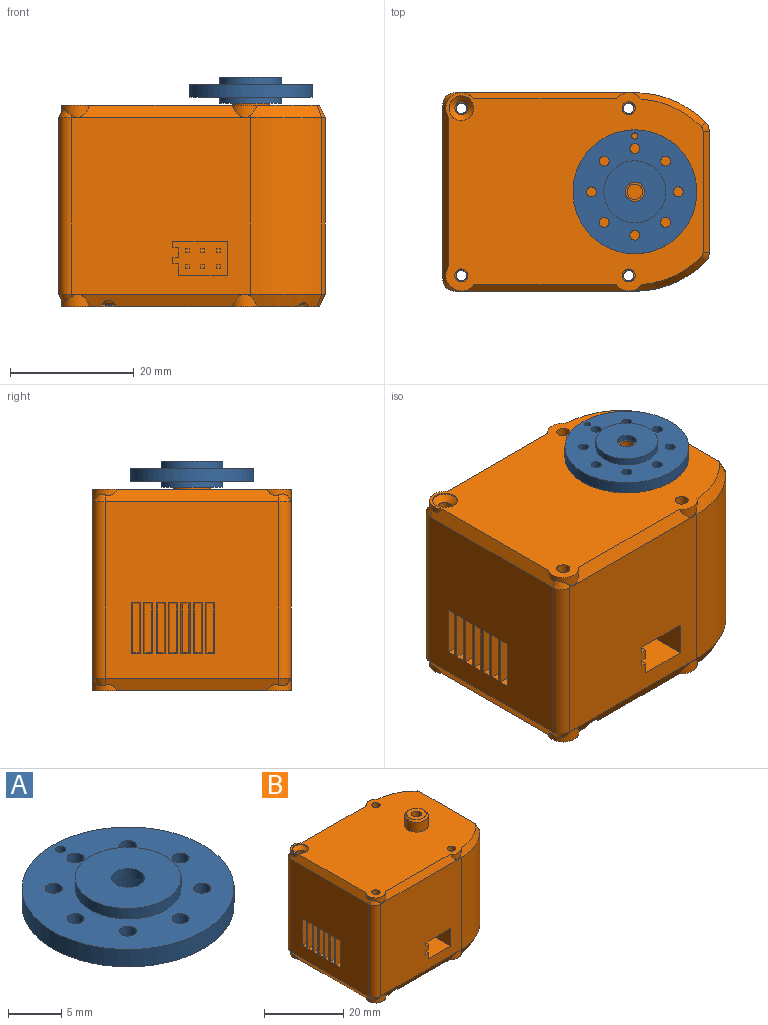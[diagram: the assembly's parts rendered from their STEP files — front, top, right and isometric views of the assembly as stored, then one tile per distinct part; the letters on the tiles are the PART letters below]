
ASSEMBLY  parts=2 mates=1
PART A: 19 faces, bbox 20x20x4.2 mm
  f0: cylinder r=5mm len=10mm, axis (0,0,-1), area 31.4mm2, adj f1,f5
  f1: plane 10x10mm, normal (0,0,-1), area 50.3mm2, adj f0,f8
  f2: cylinder r=5mm len=10mm, axis (0,0,1), area 37.7mm2, adj f3,f6
  f3: plane 10x10mm, normal (0,0,1), area 71mm2, adj f2,f7
  f4: cylinder r=10mm len=20mm, axis (0,0,1), area 125.7mm2, adj f5,f6
  f5: plane 20x20mm, normal (0,0,-1), area 218.7mm2, adj f0,f4,f10,f11,f12,f13,f14,f15
  f6: plane 20x20mm, normal (0,0,1), area 218.7mm2, adj f2,f4,f10,f11,f12,f13,f14,f15
  f7: cylinder r=1.55mm len=3.1mm, axis (0,0,1), area 9.7mm2, adj f3,f9
  f8: cylinder r=3mm len=6mm, axis (0,0,1), area 60.3mm2, adj f1,f9
  f9: plane 6x6mm, normal (0,0,-1), area 20.7mm2, adj f7,f8
  f10: cylinder r=0.8mm len=2mm, axis (0,0,1), area 10.1mm2, adj f5,f6
  f11: cylinder r=0.5mm len=2mm, axis (0,0,1), area 6.3mm2, adj f5,f6
  f12: cylinder r=0.8mm len=2mm, axis (0,0,1), area 10.1mm2, adj f5,f6
  f13: cylinder r=0.8mm len=2mm, axis (0,0,1), area 10.1mm2, adj f5,f6
  f14: cylinder r=0.8mm len=2mm, axis (0,0,1), area 10.1mm2, adj f5,f6
  f15: cylinder r=0.8mm len=2mm, axis (0,0,1), area 10.1mm2, adj f5,f6
  f16: cylinder r=0.8mm len=2mm, axis (0,0,1), area 10.1mm2, adj f5,f6
  f17: cylinder r=0.8mm len=2mm, axis (0,0,1), area 10.1mm2, adj f5,f6
  f18: cylinder r=0.8mm len=2mm, axis (0,0,1), area 10.1mm2, adj f5,f6
PART B: 273 faces, bbox 43.9x32.9x36.9 mm
  f0: cylinder r=1.05mm len=8mm, axis (0,0,-1), area 52.8mm2, adj f30,f40
  f1: cylinder r=1.05mm len=8mm, axis (0,0,-1), area 52.8mm2, adj f30,f41
  f2: cylinder r=2mm len=4mm, axis (0,0,1), area 2.5mm2, adj f6,f30
  f3: cylinder r=1.05mm len=8mm, axis (0,0,-1), area 52.8mm2, adj f30,f42
  f4: cylinder r=3mm len=6mm, axis (0,0,1), area 56.5mm2, adj f30,f43,f44
  f5: cylinder r=2.5mm len=4.5mm, axis (0,0,-1), area 8.1mm2, adj f30,f31,f32,f46,f47
  f6: cone r=1000mm half-angle=45deg, axis (0,0,1), area 12.9mm2, adj f2,f9
  f7: cylinder r=0.85mm len=20.8mm, axis (0,0,1), area 111.1mm2, adj f40,f64
  f8: cylinder r=0.85mm len=20.8mm, axis (0,0,1), area 111.1mm2, adj f41,f65
  f9: cylinder r=1.05mm len=6.85mm, axis (0,0,-1), area 45.2mm2, adj f6,f66
  f10: cylinder r=0.85mm len=20.8mm, axis (0,0,1), area 111.1mm2, adj f42,f67
  f11: cylinder r=1.25mm len=9mm, axis (0,0,-1), area 70.7mm2, adj f59,f120
  f12: cylinder r=1.05mm len=3.7mm, axis (0,0,-1), area 24.4mm2, adj f64,f146
  f13: cylinder r=1.05mm len=3.7mm, axis (0,0,-1), area 24.4mm2, adj f65,f146
  f14: cylinder r=0.85mm len=20.8mm, axis (0,0,1), area 111.1mm2, adj f66,f147
  f15: cylinder r=1.05mm len=3.7mm, axis (0,0,-1), area 24.4mm2, adj f67,f146
  f16: cylinder r=2mm len=4mm, axis (0,0,-1), area 17.4mm2, adj f135,f146,f164
  f17: cylinder r=2mm len=4mm, axis (0,0,-1), area 17.8mm2, adj f137,f146,f165
  f18: cylinder r=2mm len=4mm, axis (0,0,-1), area 18.8mm2, adj f139,f146,f166
  f19: cylinder r=2mm len=4mm, axis (0,0,-1), area 17.4mm2, adj f144,f146,f187
  f20: cylinder r=4.25mm len=8.5mm, axis (0,0,-1), area 13.4mm2, adj f146,f188
  f21: cylinder r=2mm len=4mm, axis (0,0,-1), area 2.5mm2, adj f23,f146
  f22: cylinder r=1.05mm len=2.55mm, axis (0,0,-1), area 16.8mm2, adj f23,f147
  f23: cone r=1000mm half-angle=45deg, axis (0,0,-1), area 12.9mm2, adj f21,f22
  f24: cylinder r=1.75mm len=3.5mm, axis (0,0,-1), area 2.2mm2, adj f164,f195,f196
  f25: cylinder r=1.75mm len=3.5mm, axis (0,0,-1), area 2.2mm2, adj f165,f197,f198
  f26: cylinder r=1.75mm len=3.5mm, axis (0,0,-1), area 2.2mm2, adj f166,f199,f200
  f27: cylinder r=1.75mm len=3.5mm, axis (0,0,-1), area 2.2mm2, adj f187,f201,f202
  f28: cylinder r=2.7mm len=5.4mm, axis (0,0,-1), area 8.5mm2, adj f188,f203
  f29: cylinder r=1.2mm len=10mm, axis (0,0,-1), area 75.4mm2, adj f203,f272
  f30: plane 41.5x32mm, normal (0,0,1), area 1159.4mm2, adj f0,f1,f2,f3,f4,f5,f31,f32
  f31: plane 28.86x2.86mm, normal (-0.89,0,0.45), area 59.2mm2, adj f5,f30,f39,f45,f46,f58
  f32: plane 27.94x2.94mm, normal (0,0.89,0.45), area 54.1mm2, adj f5,f30,f33,f48
  f33: cylinder r=2.5mm len=4.03mm, axis (0,0,-1), area 5.2mm2, adj f30,f32,f34,f49
  f34: cone r=14.9mm half-angle=26.6deg, axis (0,0,-1), area 26.7mm2, adj f30,f33,f49,f50,f51
  f35: plane 19.6x2mm, normal (0.89,0,0.45), area 43.8mm2, adj f30,f51,f52,f53
  f36: cone r=14.9mm half-angle=26.6deg, axis (0,0,-1), area 26.7mm2, adj f30,f37,f52,f54,f55
  f37: cylinder r=2.5mm len=4.03mm, axis (0,0,-1), area 5.2mm2, adj f30,f36,f38,f55
  f38: plane 27.94x2.94mm, normal (0,-0.89,0.45), area 54.1mm2, adj f30,f37,f39,f56
  f39: cylinder r=2.5mm len=4.5mm, axis (0,0,-1), area 8.1mm2, adj f30,f31,f38,f57,f58
  f40: plane 2.1x2.1mm, normal (0,0,1), area 1.2mm2, adj f0,f7
  f41: plane 2.1x2.1mm, normal (0,0,1), area 1.2mm2, adj f1,f8
  f42: plane 2.1x2.1mm, normal (0,0,1), area 1.2mm2, adj f3,f10
  f43: revolved ~6x3mm, area 6.1mm2, adj f4,f44,f59
  f44: revolved ~6x3mm, area 6.1mm2, adj f4,f43,f59
  f45: plane 28.5x28mm, normal (-1,0,0), area 713.8mm2, adj f31,f60,f61,f68,f69,f70,f71,f72
  f46: cone r=1.16mm half-angle=26.6deg, axis (0,0,-1), area 3.1mm2, adj f5,f31,f47,f61
  f47: plane 1.21x0.62mm, normal (0,0.89,0.45), area 0.2mm2, adj f5,f46,f48
  f48: plane 29x28.5mm, normal (0,1,0), area 766.3mm2, adj f32,f47,f49,f50,f61,f96,f97,f98
  f49: plane 1.21x0.62mm, normal (0,0.89,0.45), area 0.2mm2, adj f33,f34,f48
  f50: cylinder r=16mm len=28.5mm, axis (0,0,-1), area 362.8mm2, adj f34,f48,f62,f137
  f51: cone r=1.16mm half-angle=26.6deg, axis (0,0,-1), area 2.6mm2, adj f30,f34,f35,f62
  f52: cone r=1.16mm half-angle=26.6deg, axis (0,0,-1), area 2.6mm2, adj f30,f35,f36,f63
  f53: plane 28.5x19.6mm, normal (1,0,0), area 558.5mm2, adj f35,f62,f63,f138
  f54: cylinder r=16mm len=28.5mm, axis (0,0,-1), area 362.8mm2, adj f36,f56,f63,f139
  f55: plane 1.21x0.62mm, normal (0,-0.89,0.45), area 0.2mm2, adj f36,f37,f56
  f56: plane 29x28.5mm, normal (0,-1,0), area 781.3mm2, adj f38,f54,f55,f57,f60,f116,f117,f118
  f57: plane 1.21x0.62mm, normal (0,-0.89,0.45), area 0.2mm2, adj f39,f56,f58
  f58: cone r=1.16mm half-angle=26.6deg, axis (0,0,-1), area 3.1mm2, adj f31,f39,f57,f60
  f59: plane 5x5mm, normal (0,0,1), area 14.7mm2, adj f11,f43,f44
  f60: cylinder r=2mm len=28.5mm, axis (0,0,-1), area 89.5mm2, adj f45,f56,f58,f148
  f61: cylinder r=2mm len=28.5mm, axis (0,0,-1), area 89.5mm2, adj f45,f46,f48,f151
  f62: cylinder r=2mm len=28.5mm, axis (0,0,-1), area 44.2mm2, adj f50,f51,f53,f153
  f63: cylinder r=2mm len=28.5mm, axis (0,0,-1), area 44.2mm2, adj f52,f53,f54,f154
  f64: plane 2.1x2.1mm, normal (0,0,-1), area 1.2mm2, adj f7,f12
  f65: plane 2.1x2.1mm, normal (0,0,-1), area 1.2mm2, adj f8,f13
  f66: plane 2.1x2.1mm, normal (0,0,1), area 1.2mm2, adj f9,f14
  f67: plane 2.1x2.1mm, normal (0,0,-1), area 1.2mm2, adj f10,f15
  f68: plane 1.7x1.46mm, normal (-0.1,0,-0.99), area 2.2mm2, adj f45,f69,f71,f121
  f69: plane 8.26x1.7mm, normal (-0.1,-0.99,0), area 13.8mm2, adj f45,f68,f70,f121
  f70: plane 1.7x1.46mm, normal (-0.1,0,0.99), area 2.2mm2, adj f45,f69,f71,f121
  f71: plane 8.26x1.7mm, normal (-0.1,0.99,0), area 13.8mm2, adj f45,f68,f70,f121
  f72: plane 1.7x1.46mm, normal (-0.1,0,-0.99), area 2.2mm2, adj f45,f73,f75,f122
  f73: plane 8.26x1.7mm, normal (-0.1,-0.99,0), area 13.8mm2, adj f45,f72,f74,f122
  f74: plane 1.7x1.46mm, normal (-0.1,0,0.99), area 2.2mm2, adj f45,f73,f75,f122
  f75: plane 8.26x1.7mm, normal (-0.1,0.99,0), area 13.8mm2, adj f45,f72,f74,f122
  f76: plane 1.7x1.46mm, normal (-0.1,0,-0.99), area 2.2mm2, adj f45,f77,f79,f123
  f77: plane 8.26x1.7mm, normal (-0.1,-0.99,0), area 13.8mm2, adj f45,f76,f78,f123
  f78: plane 1.7x1.46mm, normal (-0.1,0,0.99), area 2.2mm2, adj f45,f77,f79,f123
  f79: plane 8.26x1.7mm, normal (-0.1,0.99,0), area 13.8mm2, adj f45,f76,f78,f123
  f80: plane 1.7x1.46mm, normal (-0.1,0,-0.99), area 2.2mm2, adj f45,f81,f83,f124
  f81: plane 8.26x1.7mm, normal (-0.1,-0.99,0), area 13.8mm2, adj f45,f80,f82,f124
  f82: plane 1.7x1.46mm, normal (-0.1,0,0.99), area 2.2mm2, adj f45,f81,f83,f124
  f83: plane 8.26x1.7mm, normal (-0.1,0.99,0), area 13.8mm2, adj f45,f80,f82,f124
  f84: plane 1.7x1.46mm, normal (-0.1,0,-0.99), area 2.2mm2, adj f45,f85,f87,f125
  f85: plane 8.26x1.7mm, normal (-0.1,-0.99,0), area 13.8mm2, adj f45,f84,f86,f125
  f86: plane 1.7x1.46mm, normal (-0.1,0,0.99), area 2.2mm2, adj f45,f85,f87,f125
  f87: plane 8.26x1.7mm, normal (-0.1,0.99,0), area 13.8mm2, adj f45,f84,f86,f125
  f88: plane 1.7x1.46mm, normal (-0.1,0,-0.99), area 2.2mm2, adj f45,f89,f91,f126
  f89: plane 8.26x1.7mm, normal (-0.1,-0.99,0), area 13.8mm2, adj f45,f88,f90,f126
  f90: plane 1.7x1.46mm, normal (-0.1,0,0.99), area 2.2mm2, adj f45,f89,f91,f126
  f91: plane 8.26x1.7mm, normal (-0.1,0.99,0), area 13.8mm2, adj f45,f88,f90,f126
  f92: plane 8.26x1.7mm, normal (-0.1,0.99,0), area 13.8mm2, adj f45,f93,f95,f127
  f93: plane 1.7x1.46mm, normal (-0.1,0,-0.99), area 2.2mm2, adj f45,f92,f94,f127
  f94: plane 8.26x1.7mm, normal (-0.1,-0.99,0), area 13.8mm2, adj f45,f93,f95,f127
  f95: plane 1.7x1.46mm, normal (-0.1,0,0.99), area 2.2mm2, adj f45,f92,f94,f127
  f96: plane 8.26x1.7mm, normal (-0.99,0.1,0), area 13.8mm2, adj f48,f97,f99,f129
  f97: plane 1.7x1.46mm, normal (0,0.1,0.99), area 2.2mm2, adj f48,f96,f98,f129
  f98: plane 8.26x1.7mm, normal (0.99,0.1,0), area 13.8mm2, adj f48,f97,f99,f129
  f99: plane 1.7x1.46mm, normal (0,0.1,-0.99), area 2.2mm2, adj f48,f96,f98,f129
  f100: plane 8.26x1.7mm, normal (-0.99,0.1,0), area 13.8mm2, adj f48,f101,f103,f130
  f101: plane 1.7x1.46mm, normal (0,0.1,0.99), area 2.2mm2, adj f48,f100,f102,f130
  f102: plane 8.26x1.7mm, normal (0.99,0.1,0), area 13.8mm2, adj f48,f101,f103,f130
  f103: plane 1.7x1.46mm, normal (0,0.1,-0.99), area 2.2mm2, adj f48,f100,f102,f130
  f104: plane 8.26x1.7mm, normal (-0.99,0.1,0), area 13.8mm2, adj f48,f105,f107,f131
  f105: plane 1.7x1.46mm, normal (0,0.1,0.99), area 2.2mm2, adj f48,f104,f106,f131
  f106: plane 8.26x1.7mm, normal (0.99,0.1,0), area 13.8mm2, adj f48,f105,f107,f131
  f107: plane 1.7x1.46mm, normal (0,0.1,-0.99), area 2.2mm2, adj f48,f104,f106,f131
  f108: plane 8.26x1.7mm, normal (-0.99,0.1,0), area 13.8mm2, adj f48,f109,f111,f132
  f109: plane 1.7x1.46mm, normal (0,0.1,0.99), area 2.2mm2, adj f48,f108,f110,f132
  f110: plane 8.26x1.7mm, normal (0.99,0.1,0), area 13.8mm2, adj f48,f109,f111,f132
  f111: plane 1.7x1.46mm, normal (0,0.1,-0.99), area 2.2mm2, adj f48,f108,f110,f132
  f112: plane 1.7x1.46mm, normal (0,0.1,-0.99), area 2.2mm2, adj f48,f113,f115,f133
  f113: plane 8.26x1.7mm, normal (-0.99,0.1,0), area 13.8mm2, adj f48,f112,f114,f133
  f114: plane 1.7x1.46mm, normal (0,0.1,0.99), area 2.2mm2, adj f48,f113,f115,f133
  f115: plane 8.26x1.7mm, normal (0.99,0.1,0), area 13.8mm2, adj f48,f112,f114,f133
  f116: plane 14.2x1.9mm, normal (1,0,0), area 27mm2, adj f56,f117,f140,f141
  f117: plane 14.2x7.9mm, normal (0,0,1), area 112.2mm2, adj f56,f116,f118,f141
  f118: plane 14.2x5.5mm, normal (-1,0,0), area 78.1mm2, adj f56,f117,f119,f141
  f119: plane 14.2x8.8mm, normal (0,0,-1), area 125mm2, adj f56,f118,f141,f142
  f120: plane 2.5x2.5mm, normal (0,0,1), area 4.9mm2, adj f11
  f121: plane 7.9x1.1mm, normal (-1,0,0), area 8.7mm2, adj f68,f69,f70,f71
  f122: plane 7.9x1.1mm, normal (-1,0,0), area 8.7mm2, adj f72,f73,f74,f75
  f123: plane 7.9x1.1mm, normal (-1,0,0), area 8.7mm2, adj f76,f77,f78,f79
  f124: plane 7.9x1.1mm, normal (-1,0,0), area 8.7mm2, adj f80,f81,f82,f83
  f125: plane 7.9x1.1mm, normal (-1,0,0), area 8.7mm2, adj f84,f85,f86,f87
  f126: plane 7.9x1.1mm, normal (-1,0,0), area 8.7mm2, adj f88,f89,f90,f91
  f127: plane 7.9x1.1mm, normal (-1,0,0), area 8.7mm2, adj f92,f93,f94,f95
  f128: plane 28.86x2.86mm, normal (-0.89,0,-0.45), area 59.2mm2, adj f45,f146,f148,f149,f150,f151
  f129: plane 7.9x1.1mm, normal (0,1,0), area 8.7mm2, adj f96,f97,f98,f99
  f130: plane 7.9x1.1mm, normal (0,1,0), area 8.7mm2, adj f100,f101,f102,f103
  f131: plane 7.9x1.1mm, normal (0,1,0), area 8.7mm2, adj f104,f105,f106,f107
  f132: plane 7.9x1.1mm, normal (0,1,0), area 8.7mm2, adj f108,f109,f110,f111
  f133: plane 7.9x1.1mm, normal (0,1,0), area 8.7mm2, adj f112,f113,f114,f115
  f134: plane 1.21x0.62mm, normal (0,0.89,-0.45), area 0.2mm2, adj f48,f150,f151
  f135: plane 27.94x2.94mm, normal (0,0.89,-0.45), area 52.1mm2, adj f16,f48,f146,f150,f152
  f136: plane 1.21x0.62mm, normal (0,0.89,-0.45), area 0.2mm2, adj f48,f137,f152
  f137: cone r=14.9mm half-angle=26.6deg, axis (0,0,1), area 25.4mm2, adj f17,f50,f136,f146,f152,f153
  f138: plane 19.6x2mm, normal (0.89,0,-0.45), area 43.8mm2, adj f53,f146,f153,f154
  f139: cone r=14.9mm half-angle=26.6deg, axis (0,0,1), area 25.6mm2, adj f18,f54,f143,f146,f154,f155
  f140: plane 14.2x0.9mm, normal (0,0,1), area 12.8mm2, adj f56,f116,f141,f156
  f141: plane 8.8x5.5mm, normal (0,-1,0), area 42.8mm2, adj f116,f117,f118,f119,f140,f142,f156,f157
  f142: plane 14.2x1mm, normal (1,0,0), area 14.2mm2, adj f56,f119,f141,f163
  f143: plane 1.21x0.62mm, normal (0,-0.89,-0.45), area 0.2mm2, adj f56,f139,f155
  f144: plane 27.94x2.94mm, normal (0,-0.89,-0.45), area 52.1mm2, adj f19,f56,f146,f149,f155
  f145: plane 1.21x0.62mm, normal (0,-0.89,-0.45), area 0.2mm2, adj f56,f148,f149
  f146: plane 41.5x32mm, normal (0,0,-1), area 1083.4mm2, adj f12,f13,f15,f16,f17,f18,f19,f20
  f147: plane 2.1x2.1mm, normal (0,0,-1), area 1.2mm2, adj f14,f22
  f148: cone r=1.16mm half-angle=26.6deg, axis (0,0,1), area 3.1mm2, adj f60,f128,f145,f149
  f149: cylinder r=2.5mm len=4.5mm, axis (0,0,1), area 8.1mm2, adj f128,f144,f145,f146,f148
  f150: cylinder r=2.5mm len=4.5mm, axis (0,0,1), area 8.1mm2, adj f128,f134,f135,f146,f151
  f151: cone r=1.16mm half-angle=26.6deg, axis (0,0,1), area 3.1mm2, adj f61,f128,f134,f150
  f152: cylinder r=2.5mm len=4.03mm, axis (0,0,1), area 5.2mm2, adj f135,f136,f137,f146
  f153: cone r=1.16mm half-angle=26.6deg, axis (0,0,1), area 2.6mm2, adj f62,f137,f138,f146
  f154: cone r=1.16mm half-angle=26.6deg, axis (0,0,1), area 2.6mm2, adj f63,f138,f139,f146
  f155: cylinder r=2.5mm len=4.03mm, axis (0,0,1), area 5.2mm2, adj f139,f143,f144,f146
  f156: plane 14.2x1mm, normal (1,0,0), area 14.2mm2, adj f56,f140,f141,f167
  f157: plane 5.7x0.64mm, normal (-1,0,0), area 3.6mm2, adj f141,f168,f169,f170
  f158: plane 5.7x0.64mm, normal (-1,0,0), area 3.6mm2, adj f141,f171,f172,f173
  f159: plane 5.7x0.64mm, normal (-1,0,0), area 3.6mm2, adj f141,f174,f175,f176
  f160: plane 5.7x0.64mm, normal (-1,0,0), area 3.6mm2, adj f141,f177,f178,f179
  f161: plane 5.7x0.64mm, normal (-1,0,0), area 3.6mm2, adj f141,f180,f181,f182
  f162: plane 5.7x0.64mm, normal (0,0,-1), area 3.6mm2, adj f141,f183,f184,f185
  f163: plane 14.2x0.9mm, normal (0,0,1), area 12.8mm2, adj f56,f141,f142,f186
  f164: plane 4x4mm, normal (0,0,-1), area 2.9mm2, adj f16,f24
  f165: plane 4x4mm, normal (0,0,-1), area 2.9mm2, adj f17,f25
  f166: plane 4x4mm, normal (0,0,-1), area 2.9mm2, adj f18,f26
  f167: plane 14.2x0.9mm, normal (0,0,-1), area 12.8mm2, adj f56,f141,f156,f186
  f168: plane 5.7x0.64mm, normal (0,0,-1), area 3.6mm2, adj f141,f157,f170,f189
  f169: plane 5.7x0.64mm, normal (0,0,1), area 3.6mm2, adj f141,f157,f170,f189
  f170: plane 0.64x0.64mm, normal (0,-1,0), area 0.4mm2, adj f157,f168,f169,f189
  f171: plane 5.7x0.64mm, normal (0,0,-1), area 3.6mm2, adj f141,f158,f173,f190
  f172: plane 5.7x0.64mm, normal (0,0,1), area 3.6mm2, adj f141,f158,f173,f190
  f173: plane 0.64x0.64mm, normal (0,-1,0), area 0.4mm2, adj f158,f171,f172,f190
  f174: plane 5.7x0.64mm, normal (0,0,-1), area 3.6mm2, adj f141,f159,f176,f191
  f175: plane 5.7x0.64mm, normal (0,0,1), area 3.6mm2, adj f141,f159,f176,f191
  f176: plane 0.64x0.64mm, normal (0,-1,0), area 0.4mm2, adj f159,f174,f175,f191
  f177: plane 5.7x0.64mm, normal (0,0,-1), area 3.6mm2, adj f141,f160,f179,f192
  f178: plane 5.7x0.64mm, normal (0,0,1), area 3.6mm2, adj f141,f160,f179,f192
  f179: plane 0.64x0.64mm, normal (0,-1,0), area 0.4mm2, adj f160,f177,f178,f192
  f180: plane 5.7x0.64mm, normal (0,0,-1), area 3.6mm2, adj f141,f161,f182,f193
  f181: plane 5.7x0.64mm, normal (0,0,1), area 3.6mm2, adj f141,f161,f182,f193
  f182: plane 0.64x0.64mm, normal (0,-1,0), area 0.4mm2, adj f161,f180,f181,f193
  f183: plane 5.7x0.64mm, normal (1,0,0), area 3.6mm2, adj f141,f162,f185,f194
  f184: plane 5.7x0.64mm, normal (-1,0,0), area 3.6mm2, adj f141,f162,f185,f194
  f185: plane 0.64x0.64mm, normal (0,-1,0), area 0.4mm2, adj f162,f183,f184,f194
  f186: plane 14.2x1.6mm, normal (1,0,0), area 22.7mm2, adj f56,f141,f163,f167
  f187: plane 4x4mm, normal (0,0,-1), area 2.9mm2, adj f19,f27
  f188: plane 8.5x8.5mm, normal (0,0,-1), area 33.8mm2, adj f20,f28
  f189: plane 5.7x0.64mm, normal (1,0,0), area 3.6mm2, adj f141,f168,f169,f170
  f190: plane 5.7x0.64mm, normal (1,0,0), area 3.6mm2, adj f141,f171,f172,f173
  f191: plane 5.7x0.64mm, normal (1,0,0), area 3.6mm2, adj f141,f174,f175,f176
  f192: plane 5.7x0.64mm, normal (1,0,0), area 3.6mm2, adj f141,f177,f178,f179
  f193: plane 5.7x0.64mm, normal (1,0,0), area 3.6mm2, adj f141,f180,f181,f182
  f194: plane 5.7x0.64mm, normal (0,0,1), area 3.6mm2, adj f141,f183,f184,f185
  f195: torus R=0.75mm, axis (0,0,1), area 6mm2, adj f24,f196,f204,f205,f206,f207,f208,f209
  f196: torus R=0.75mm, axis (0,0,1), area 6mm2, adj f24,f195,f209,f210,f213,f214,f215,f216
  f197: torus R=0.75mm, axis (0,0,1), area 6mm2, adj f25,f198,f220,f221,f222,f223,f224,f225
  f198: torus R=0.75mm, axis (0,0,1), area 6mm2, adj f25,f197,f225,f226,f229,f230,f231,f232
  f199: torus R=0.75mm, axis (0,0,1), area 6mm2, adj f26,f200,f236,f237,f238,f239,f240,f241
  f200: torus R=0.75mm, axis (0,0,1), area 6mm2, adj f26,f199,f236,f244,f245,f246,f247,f248
  f201: torus R=0.75mm, axis (0,0,1), area 6mm2, adj f27,f202,f252,f253,f254,f255,f256,f257
  f202: torus R=0.75mm, axis (0,0,1), area 6mm2, adj f27,f201,f252,f260,f261,f262,f263,f264
  f203: plane 5.4x5.4mm, normal (0,0,-1), area 18.4mm2, adj f28,f29
  f204: plane 0.82x0.64mm, normal (0.92,0.38,0), area 0.5mm2, adj f195,f205,f211,f212,f268
  f205: plane 0.49x0.41mm, normal (0.38,-0.92,0), area 0.2mm2, adj f195,f204,f206,f268
  f206: plane 0.81x0.64mm, normal (-0.92,-0.38,0), area 0.5mm2, adj f195,f205,f207,f208,f268
  f207: sphere r=3.75mm, area 0.3mm2, adj f195,f206,f208
  f208: plane 0.82x0.64mm, normal (0.38,-0.92,0), area 0.5mm2, adj f195,f206,f207,f209,f268
  f209: plane 0.49x0.42mm, normal (-0.92,-0.38,0), area 0.2mm2, adj f195,f196,f208,f213,f268
  f210: plane 0.49x0.42mm, normal (0.92,0.38,0), area 0.2mm2, adj f195,f196,f211,f219,f268
  f211: plane 0.81x0.64mm, normal (0.38,-0.92,0), area 0.5mm2, adj f195,f204,f210,f212,f268
  f212: sphere r=3.75mm, area 0.3mm2, adj f195,f204,f211
  f213: plane 0.81x0.64mm, normal (-0.38,0.92,0), area 0.5mm2, adj f196,f209,f214,f215,f268
  f214: sphere r=3.75mm, area 0.3mm2, adj f196,f213,f215
  f215: plane 0.82x0.64mm, normal (-0.92,-0.38,0), area 0.5mm2, adj f196,f213,f214,f216,f268
  f216: plane 0.49x0.41mm, normal (-0.38,0.92,0), area 0.2mm2, adj f196,f215,f217,f268
  f217: plane 0.81x0.64mm, normal (0.92,0.38,0), area 0.5mm2, adj f196,f216,f218,f219,f268
  f218: sphere r=3.75mm, area 0.3mm2, adj f196,f217,f219
  f219: plane 0.82x0.64mm, normal (-0.38,0.92,0), area 0.5mm2, adj f196,f210,f217,f218,f268
  f220: plane 0.82x0.64mm, normal (0.92,0.38,0), area 0.5mm2, adj f197,f221,f227,f228,f269
  f221: plane 0.49x0.41mm, normal (0.38,-0.92,0), area 0.2mm2, adj f197,f220,f222,f269
  f222: plane 0.81x0.64mm, normal (-0.92,-0.38,0), area 0.5mm2, adj f197,f221,f223,f224,f269
  f223: sphere r=3.75mm, area 0.3mm2, adj f197,f222,f224
  f224: plane 0.82x0.64mm, normal (0.38,-0.92,0), area 0.5mm2, adj f197,f222,f223,f225,f269
  f225: plane 0.49x0.42mm, normal (-0.92,-0.38,0), area 0.2mm2, adj f197,f198,f224,f229,f269
  f226: plane 0.49x0.42mm, normal (0.92,0.38,0), area 0.2mm2, adj f197,f198,f227,f235,f269
  f227: plane 0.81x0.64mm, normal (0.38,-0.92,0), area 0.5mm2, adj f197,f220,f226,f228,f269
  f228: sphere r=3.75mm, area 0.3mm2, adj f197,f220,f227
  f229: plane 0.81x0.64mm, normal (-0.38,0.92,0), area 0.5mm2, adj f198,f225,f230,f231,f269
  f230: sphere r=3.75mm, area 0.3mm2, adj f198,f229,f231
  f231: plane 0.82x0.64mm, normal (-0.92,-0.38,0), area 0.5mm2, adj f198,f229,f230,f232,f269
  f232: plane 0.49x0.41mm, normal (-0.38,0.92,0), area 0.2mm2, adj f198,f231,f233,f269
  f233: plane 0.81x0.64mm, normal (0.92,0.38,0), area 0.5mm2, adj f198,f232,f234,f235,f269
  f234: sphere r=3.75mm, area 0.3mm2, adj f198,f233,f235
  f235: plane 0.82x0.64mm, normal (-0.38,0.92,0), area 0.5mm2, adj f198,f226,f233,f234,f269
  f236: plane 0.49x0.42mm, normal (-0.92,-0.38,0), area 0.2mm2, adj f199,f200,f237,f249,f270
  f237: plane 0.81x0.64mm, normal (-0.38,0.92,0), area 0.5mm2, adj f199,f236,f238,f239,f270
  f238: sphere r=3.75mm, area 0.3mm2, adj f199,f237,f239
  f239: plane 0.82x0.64mm, normal (-0.92,-0.38,0), area 0.5mm2, adj f199,f237,f238,f240,f270
  f240: plane 0.49x0.41mm, normal (-0.38,0.92,0), area 0.2mm2, adj f199,f239,f241,f270
  f241: plane 0.81x0.64mm, normal (0.92,0.38,0), area 0.5mm2, adj f199,f240,f242,f243,f270
  f242: sphere r=3.75mm, area 0.3mm2, adj f199,f241,f243
  f243: plane 0.82x0.64mm, normal (-0.38,0.92,0), area 0.5mm2, adj f199,f241,f242,f244,f270
  f244: plane 0.49x0.42mm, normal (0.92,0.38,0), area 0.2mm2, adj f199,f200,f243,f250,f270
  f245: plane 0.82x0.64mm, normal (0.92,0.38,0), area 0.5mm2, adj f200,f246,f250,f251,f270
  f246: plane 0.49x0.41mm, normal (0.38,-0.92,0), area 0.2mm2, adj f200,f245,f247,f270
  f247: plane 0.81x0.64mm, normal (-0.92,-0.38,0), area 0.5mm2, adj f200,f246,f248,f249,f270
  f248: sphere r=3.75mm, area 0.3mm2, adj f200,f247,f249
  f249: plane 0.82x0.64mm, normal (0.38,-0.92,0), area 0.5mm2, adj f200,f236,f247,f248,f270
  f250: plane 0.81x0.64mm, normal (0.38,-0.92,0), area 0.5mm2, adj f200,f244,f245,f251,f270
  f251: sphere r=3.75mm, area 0.3mm2, adj f200,f245,f250
  f252: plane 0.49x0.42mm, normal (-0.92,-0.38,0), area 0.2mm2, adj f201,f202,f253,f265,f271
  f253: plane 0.81x0.64mm, normal (-0.38,0.92,0), area 0.5mm2, adj f201,f252,f254,f255,f271
  f254: sphere r=3.75mm, area 0.3mm2, adj f201,f253,f255
  f255: plane 0.82x0.64mm, normal (-0.92,-0.38,0), area 0.5mm2, adj f201,f253,f254,f256,f271
  f256: plane 0.49x0.41mm, normal (-0.38,0.92,0), area 0.2mm2, adj f201,f255,f257,f271
  f257: plane 0.81x0.64mm, normal (0.92,0.38,0), area 0.5mm2, adj f201,f256,f258,f259,f271
  f258: sphere r=3.75mm, area 0.3mm2, adj f201,f257,f259
  f259: plane 0.82x0.64mm, normal (-0.38,0.92,0), area 0.5mm2, adj f201,f257,f258,f260,f271
  f260: plane 0.49x0.42mm, normal (0.92,0.38,0), area 0.2mm2, adj f201,f202,f259,f266,f271
  f261: plane 0.82x0.64mm, normal (0.92,0.38,0), area 0.5mm2, adj f202,f262,f266,f267,f271
  f262: plane 0.49x0.41mm, normal (0.38,-0.92,0), area 0.2mm2, adj f202,f261,f263,f271
  f263: plane 0.81x0.64mm, normal (-0.92,-0.38,0), area 0.5mm2, adj f202,f262,f264,f265,f271
  f264: sphere r=3.75mm, area 0.3mm2, adj f202,f263,f265
  f265: plane 0.82x0.64mm, normal (0.38,-0.92,0), area 0.5mm2, adj f202,f252,f263,f264,f271
  f266: plane 0.81x0.64mm, normal (0.38,-0.92,0), area 0.5mm2, adj f202,f260,f261,f267,f271
  f267: sphere r=3.75mm, area 0.3mm2, adj f202,f261,f266
  f268: plane 2.2x2.2mm, normal (0,0,-1), area 1.7mm2, adj f204,f205,f206,f208,f209,f210,f211,f213
  f269: plane 2.2x2.2mm, normal (0,0,-1), area 1.7mm2, adj f220,f221,f222,f224,f225,f226,f227,f229
  f270: plane 2.2x2.2mm, normal (0,0,-1), area 1.7mm2, adj f236,f237,f239,f240,f241,f243,f244,f245
  f271: plane 2.2x2.2mm, normal (0,0,-1), area 1.7mm2, adj f252,f253,f255,f256,f257,f259,f260,f261
  f272: plane 2.4x2.4mm, normal (0,0,-1), area 4.5mm2, adj f29
PLACE A t=(7.44,-7.02,-10.75)mm
PLACE B t=(7.44,-7.02,9.25)mm
MATE fastened A.f0 <-> B.f11  axis (0,0,-1) through (7.44,-7.02,9.25)mm
